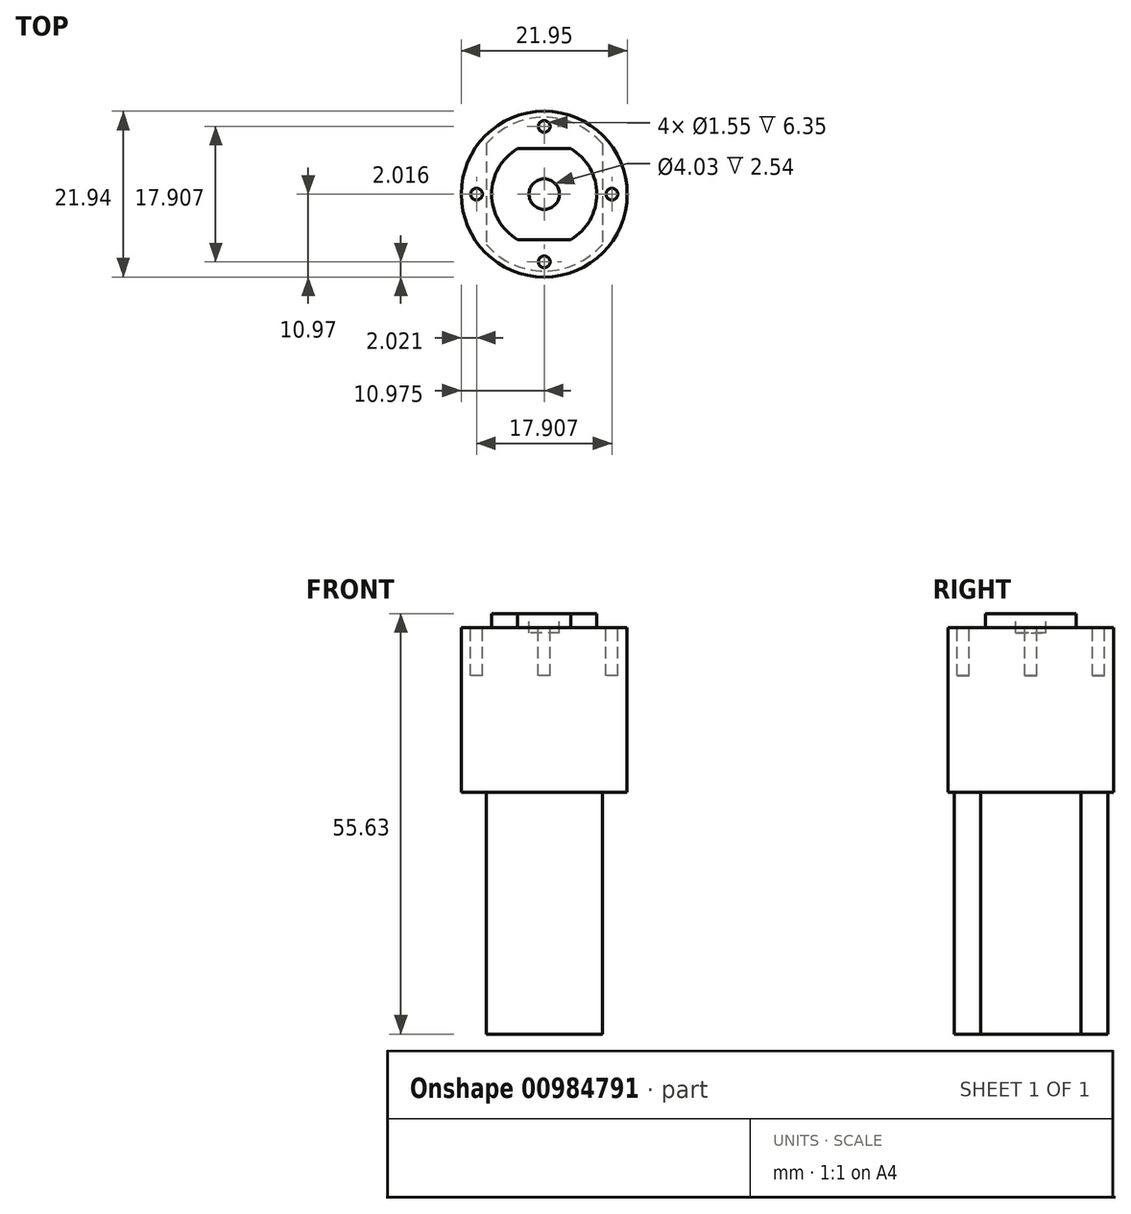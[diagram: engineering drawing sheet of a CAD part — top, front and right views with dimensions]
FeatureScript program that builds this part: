
annotation { "Feature Type Name" : "Feature", "Feature Type Description" : "" }
export const myFeature = defineFeature(function(context is Context, id is Id, definition is map)
    precondition{}
    {
        {
            var Q0;
            Q0=qCreatedBy(makeId("Top.planeOp"),FACE);
            var sketch = newSketch(context, id + "F0", { "sketchPlane" : qUnion([Q0])});
            skCircle(sketch, "E0", {"center": v(-29.49, 20.49) * mm, "radius": 10.97 * mm});
            skSolve(sketch);
        }
        {
            var Q0;
            Q0=makeQuery(id+"F0.imprint","IMPRINT",FACE,{"disambiguationData":[TD([[makeQuery(id+"F0.imprint","IMPRINT",EDGE,{"derivedFrom":sQuery(id+"F0.wireOp",EDGE,"E0")}),1.0]])]});
            extrude(context, id + "F1", {"entities" : qUnion([Q0]), "depth" : 21.78 * mm, "offsetDistance" : 25.4 * mm});
        }
        {
            var Q0;
            Q0=makeQuery(id+"F1.opExtrude","CAP_FACE",FACE,{"disambiguationData":[OSD([sQuery(id+"F0.wireOp",EDGE,"E0")])],"isStart":false});
            var sketch = newSketch(context, id + "F2", { "sketchPlane" : qUnion([Q0])});
            skLineSegment(sketch, "E1", {"start": v(-29.49, 20.49) * mm, "end": v(-29.49, -51.55) * mm, "construction": true});
            skLineSegment(sketch, "E2", {"start": v(-29.49, 20.49) * mm, "end": v(-92.58, 20.49) * mm, "construction": true});
            skCircle(sketch, "E3", {"center": v(-29.49, 29.44) * mm, "radius": 0.77 * mm});
            skCircle(sketch, "E4.1.0", {"center": v(-38.44, 20.49) * mm, "radius": 0.77 * mm});
            skCircle(sketch, "E4.2.0", {"center": v(-29.49, 11.54) * mm, "radius": 0.77 * mm});
            skCircle(sketch, "E4.3.0", {"center": v(-20.53, 20.49) * mm, "radius": 0.77 * mm});
            skPoint(sketch, "E4.center", {"position": v(-29.49, 20.49) * mm});
            skSolve(sketch);
        }
        {
            var Q0;
            Q0=makeQuery(id+"F2.imprint","IMPRINT",FACE,{"disambiguationData":[TD([[makeQuery(id+"F2.imprint","IMPRINT",EDGE,{"derivedFrom":sQuery(id+"F2.wireOp",EDGE,"E4.1.0")}),1.0]])]});
            var Q1;
            Q1=makeQuery(id+"F2.imprint","IMPRINT",FACE,{"disambiguationData":[TD([[makeQuery(id+"F2.imprint","IMPRINT",EDGE,{"derivedFrom":sQuery(id+"F2.wireOp",EDGE,"E4.2.0")}),1.0]])]});
            var Q2;
            Q2=makeQuery(id+"F2.imprint","IMPRINT",FACE,{"disambiguationData":[TD([[makeQuery(id+"F2.imprint","IMPRINT",EDGE,{"derivedFrom":sQuery(id+"F2.wireOp",EDGE,"E4.3.0")}),1.0]])]});
            var Q3;
            Q3=makeQuery(id+"F2.imprint","IMPRINT",FACE,{"disambiguationData":[TD([[makeQuery(id+"F2.imprint","IMPRINT",EDGE,{"derivedFrom":sQuery(id+"F2.wireOp",EDGE,"E3")}),1.0]])]});
            extrude(context, id + "F3", {"entities" : qUnion([Q0, Q1, Q2, Q3]), "operationType" : NewBodyOperationType.REMOVE, "oppositeDirection" : true, "depth" : 6.35 * mm, "offsetDistance" : 25.4 * mm});
        }
        {
            var Q0;
            Q0=makeQuery(id+"F1.opExtrude","CAP_FACE",FACE,{"disambiguationData":[OSD([sQuery(id+"F0.wireOp",EDGE,"E0")])],"isStart":false});
            var sketch = newSketch(context, id + "F4", { "sketchPlane" : qUnion([Q0])});
            skLineSegment(sketch, "E5", {"start": v(-29.49, 20.49) * mm, "end": v(-40.46, 20.49) * mm, "construction": true});
            skLineSegment(sketch, "E6", {"start": v(-29.49, 20.49) * mm, "end": v(-29.49, 9.52) * mm, "construction": true});
            skArc(sketch, "E7", {"start": v(-25.97, 14.48) * mm, "mid": v(-22.53, 20.49) * mm, "end": v(-25.97, 26.5) * mm});
            skLineSegment(sketch, "E8.bottom", {"start": v(-25.97, 14.48) * mm, "end": v(-33, 14.48) * mm});
            skLineSegment(sketch, "E8.top", {"start": v(-25.97, 26.5) * mm, "end": v(-33, 26.5) * mm});
            skArc(sketch, "E9.trimOffspring", {"start": v(-33, 26.5) * mm, "mid": v(-36.44, 20.49) * mm, "end": v(-33, 14.48) * mm});
            skSolve(sketch);
        }
        {
            var Q0;
            Q0=makeQuery(id+"F4.imprint","IMPRINT",FACE,{"disambiguationData":[TD([[makeQuery(id+"F4.imprint","IMPRINT",EDGE,{"derivedFrom":sQuery(id+"F4.wireOp",EDGE,"E7")}),1.0]])]});
            extrude(context, id + "F5", {"entities" : qUnion([Q0]), "operationType" : NewBodyOperationType.ADD, "depth" : 1.87 * mm, "offsetDistance" : 25.4 * mm});
        }
        {
            var Q0;
            Q0=makeQuery(id+"F5.opExtrude","CAP_FACE",FACE,{"disambiguationData":[OSD([sQuery(id+"F4.wireOp",EDGE,"E7"),sQuery(id+"F4.wireOp",EDGE,"E8.bottom"),sQuery(id+"F4.wireOp",EDGE,"E8.top"),sQuery(id+"F4.wireOp",EDGE,"E9.trimOffspring")])],"isStart":false});
            var sketch = newSketch(context, id + "F6", { "sketchPlane" : qUnion([Q0])});
            skLineSegment(sketch, "E10", {"start": v(-29.49, 20.49) * mm, "end": v(-36.44, 20.49) * mm, "construction": true});
            skCircle(sketch, "E11", {"center": v(-29.49, 20.49) * mm, "radius": 2.01 * mm});
            skSolve(sketch);
        }
        {
            var Q0;
            Q0=makeQuery(id+"F6.imprint","IMPRINT",FACE,{"disambiguationData":[TD([[makeQuery(id+"F6.imprint","IMPRINT",EDGE,{"derivedFrom":sQuery(id+"F6.wireOp",EDGE,"E11")}),1.0]])]});
            extrude(context, id + "F7", {"entities" : qUnion([Q0]), "operationType" : NewBodyOperationType.REMOVE, "oppositeDirection" : true, "depth" : 2.54 * mm, "offsetDistance" : 25.4 * mm});
        }
        {
            var Q0;
            Q0=makeQuery(id+"F1.opExtrude","CAP_FACE",FACE,{"disambiguationData":[OSD([sQuery(id+"F0.wireOp",EDGE,"E0")])],"isStart":true});
            var sketch = newSketch(context, id + "F8", { "sketchPlane" : qUnion([Q0])});
            skLineSegment(sketch, "E12", {"start": v(-29.49, -20.49) * mm, "end": v(-40.46, -20.49) * mm, "construction": true});
            skLineSegment(sketch, "E13", {"start": v(-29.49, -20.49) * mm, "end": v(-29.49, -9.52) * mm, "construction": true});
            skCircle(sketch, "E14", {"center": v(-29.49, -20.49) * mm, "radius": 10.16 * mm});
            skLineSegment(sketch, "E15.bottom", {"start": v(-37.17, -27.14) * mm, "end": v(-21.8, -27.14) * mm});
            skLineSegment(sketch, "E15.top", {"start": v(-37.17, -13.84) * mm, "end": v(-21.8, -13.84) * mm});
            skLineSegment(sketch, "E15.left", {"start": v(-37.17, -27.14) * mm, "end": v(-37.17, -13.84) * mm});
            skLineSegment(sketch, "E15.right", {"start": v(-21.8, -27.14) * mm, "end": v(-21.8, -13.84) * mm});
            skSolve(sketch);
        }
        {
            var Q0;
            {var subQ0=sQuery(id+"F8.wireOp",EDGE,"E15.bottom");Q0=makeQuery(id+"F8.imprint","IMPRINT",FACE,{"disambiguationData":[TD([[makeQuery(id+"F8.imprint","IMPRINT",EDGE,{"derivedFrom":subQ0}),-1.0]])]});}
            var Q1;
            Q1=makeQuery(id+"F8.imprint","IMPRINT",FACE,{"disambiguationData":[TD([[makeQuery(id+"F8.imprint","IMPRINT",EDGE,{"derivedFrom":sQuery(id+"F8.wireOp",EDGE,"E15.bottom")}),1.0]])]});
            var Q2;
            {var subQ0=sQuery(id+"F8.wireOp",EDGE,"E15.top");Q2=makeQuery(id+"F8.imprint","IMPRINT",FACE,{"disambiguationData":[TD([[makeQuery(id+"F8.imprint","IMPRINT",EDGE,{"derivedFrom":subQ0}),1.0]])]});}
            extrude(context, id + "F9", {"entities" : qUnion([Q0, Q1, Q2]), "operationType" : NewBodyOperationType.ADD, "depth" : 31.98 * mm, "offsetDistance" : 25.4 * mm});
        }
    });
